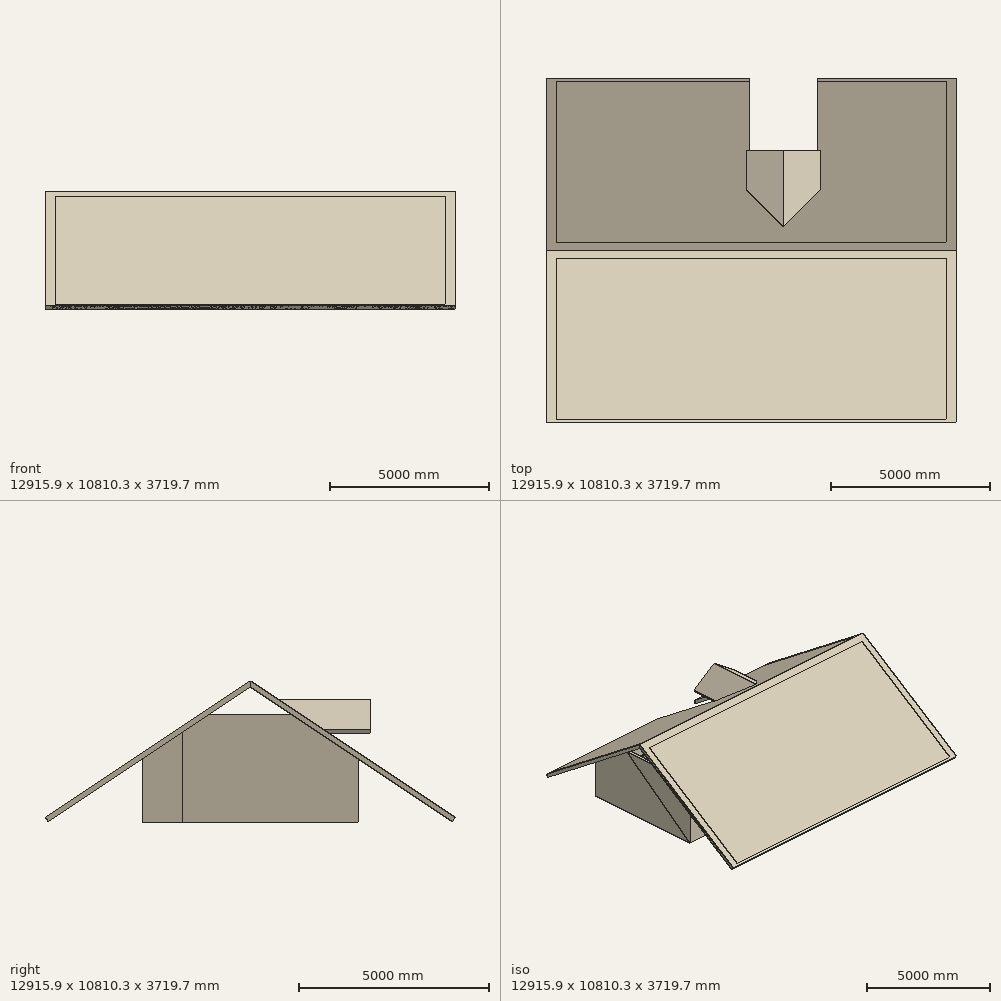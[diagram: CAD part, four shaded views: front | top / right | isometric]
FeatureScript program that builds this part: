
annotation { "Feature Type Name" : "Feature", "Feature Type Description" : "" }
export const myFeature = defineFeature(function(context is Context, id is Id, definition is map)
    precondition{}
    {
        {
            var Q0;
            Q0=qCreatedBy(makeId("Top.planeOp"),FACE);
            cPlane(context, id + "F0", {"entities" : qUnion([Q0]), "cplaneType" : CPlaneType.OFFSET, "offset" : 1 / 406.4 * mm, "oppositeDirection" : true, "width" : 152.4 * mm, "height" : 152.4 * mm});
        }
        {
            var Q0;
            Q0=qCreatedBy(makeId("Top.planeOp"),FACE);
            var sketch = newSketch(context, id + "F1", { "sketchPlane" : qUnion([Q0])});
            skLineSegment(sketch, "E0", {"start": v(0, 0) * mm, "end": v(0, 5448.3) * mm});
            skLineSegment(sketch, "E1", {"start": v(0, 5448.3) * mm, "end": v(12306.3, 5448.3) * mm});
            skLineSegment(sketch, "E2", {"start": v(12306.3, 5448.3) * mm, "end": v(12306.3, 800.1) * mm});
            skLineSegment(sketch, "E3", {"start": v(12306.3, 800.1) * mm, "end": v(9880.6, 800.1) * mm});
            skLineSegment(sketch, "E4", {"start": v(9880.6, 800.1) * mm, "end": v(9880.6, -254) * mm});
            skLineSegment(sketch, "E5", {"start": v(9880.6, -254) * mm, "end": v(3975.1, -254) * mm});
            skLineSegment(sketch, "E6", {"start": v(3975.1, -254) * mm, "end": v(3975.1, 1689.1) * mm});
            skLineSegment(sketch, "E7", {"start": v(3975.1, 1689.1) * mm, "end": v(2006.6, 1689.1) * mm});
            skLineSegment(sketch, "E8", {"start": v(2006.6, 1689.1) * mm, "end": v(2006.6, 0) * mm});
            skLineSegment(sketch, "E9", {"start": v(2006.6, 0) * mm, "end": v(0, 0) * mm});
            skLineSegment(sketch, "E10.0", {"start": v(12153.9, 5295.9) * mm, "end": v(12153.9, 952.5) * mm, "construction": true});
            skLineSegment(sketch, "E10.1", {"start": v(152.4, 5295.9) * mm, "end": v(12153.9, 5295.9) * mm, "construction": true});
            skLineSegment(sketch, "E10.2", {"start": v(12153.9, 952.5) * mm, "end": v(9728.2, 952.5) * mm, "construction": true});
            skLineSegment(sketch, "E10.3", {"start": v(152.4, 152.4) * mm, "end": v(152.4, 5295.9) * mm, "construction": true});
            skLineSegment(sketch, "E10.4", {"start": v(1854.2, 152.4) * mm, "end": v(152.4, 152.4) * mm, "construction": true});
            skLineSegment(sketch, "E10.5", {"start": v(1854.2, 1841.5) * mm, "end": v(1854.2, 152.4) * mm, "construction": true});
            skLineSegment(sketch, "E10.6", {"start": v(9728.2, 952.5) * mm, "end": v(9728.2, -101.6) * mm, "construction": true});
            skLineSegment(sketch, "E10.7", {"start": v(9728.2, -101.6) * mm, "end": v(4127.5, -101.6) * mm, "construction": true});
            skLineSegment(sketch, "E10.8", {"start": v(4127.5, -101.6) * mm, "end": v(4127.5, 1841.5) * mm, "construction": true});
            skLineSegment(sketch, "E10.9", {"start": v(4127.5, 1841.5) * mm, "end": v(1854.2, 1841.5) * mm, "construction": true});
            skLineSegment(sketch, "E11", {"start": v(0, 0) * mm, "end": v(0, -114.3) * mm, "construction": true});
            skLineSegment(sketch, "E12.bottom", {"start": v(7023.1, -101.6) * mm, "end": v(7137.4, -101.6) * mm, "construction": true});
            skLineSegment(sketch, "E12.top", {"start": v(7023.1, 3365.5) * mm, "end": v(7137.4, 3365.5) * mm, "construction": true});
            skLineSegment(sketch, "E12.left", {"start": v(7023.1, -101.6) * mm, "end": v(7023.1, 3365.5) * mm, "construction": true});
            skLineSegment(sketch, "E12.right", {"start": v(7137.4, -101.6) * mm, "end": v(7137.4, 3365.5) * mm, "construction": true});
            skLineSegment(sketch, "E13.bottom", {"start": v(7137.4, 2730.5) * mm, "end": v(9728.2, 2730.5) * mm, "construction": true});
            skLineSegment(sketch, "E13.top", {"start": v(7137.4, 2616.2) * mm, "end": v(9728.2, 2616.2) * mm, "construction": true});
            skLineSegment(sketch, "E13.left", {"start": v(7137.4, 2730.5) * mm, "end": v(7137.4, 2616.2) * mm, "construction": true});
            skLineSegment(sketch, "E13.right", {"start": v(9728.2, 2730.5) * mm, "end": v(9728.2, 2616.2) * mm, "construction": true});
            skLineSegment(sketch, "E14.bottom", {"start": v(9728.2, 952.5) * mm, "end": v(9842.5, 952.5) * mm, "construction": true});
            skLineSegment(sketch, "E14.top", {"start": v(9728.2, 3263.9) * mm, "end": v(9842.5, 3263.9) * mm, "construction": true});
            skLineSegment(sketch, "E14.left", {"start": v(9728.2, 952.5) * mm, "end": v(9728.2, 3263.9) * mm, "construction": true});
            skLineSegment(sketch, "E14.right", {"start": v(9842.5, 952.5) * mm, "end": v(9842.5, 3263.9) * mm, "construction": true});
            skLineSegment(sketch, "E15.bottom", {"start": v(9728.2, 5295.9) * mm, "end": v(9842.5, 5295.9) * mm, "construction": true});
            skLineSegment(sketch, "E15.top", {"start": v(9728.2, 3873.5) * mm, "end": v(9842.5, 3873.5) * mm, "construction": true});
            skLineSegment(sketch, "E15.left", {"start": v(9728.2, 5295.9) * mm, "end": v(9728.2, 3873.5) * mm, "construction": true});
            skLineSegment(sketch, "E15.right", {"start": v(9842.5, 5295.9) * mm, "end": v(9842.5, 3873.5) * mm, "construction": true});
            skLineSegment(sketch, "E16.bottom", {"start": v(12153.9, 2235.2) * mm, "end": v(11239.5, 2235.2) * mm, "construction": true});
            skLineSegment(sketch, "E16.top", {"start": v(12153.9, 2120.9) * mm, "end": v(11239.5, 2120.9) * mm, "construction": true});
            skLineSegment(sketch, "E16.left", {"start": v(12153.9, 2235.2) * mm, "end": v(12153.9, 2120.9) * mm, "construction": true});
            skLineSegment(sketch, "E16.right", {"start": v(11239.5, 2235.2) * mm, "end": v(11239.5, 2120.9) * mm, "construction": true});
            skLineSegment(sketch, "E17.bottom", {"start": v(10439.4, 952.5) * mm, "end": v(10553.7, 952.5) * mm, "construction": true});
            skLineSegment(sketch, "E17.top", {"start": v(10439.4, 2260.6) * mm, "end": v(10553.7, 2260.6) * mm, "construction": true});
            skLineSegment(sketch, "E17.left", {"start": v(10439.4, 952.5) * mm, "end": v(10439.4, 2260.6) * mm, "construction": true});
            skLineSegment(sketch, "E17.right", {"start": v(10553.7, 952.5) * mm, "end": v(10553.7, 2260.6) * mm, "construction": true});
            skLineSegment(sketch, "E18.bottom", {"start": v(10553.7, 2260.6) * mm, "end": v(9842.5, 2260.6) * mm, "construction": true});
            skLineSegment(sketch, "E18.top", {"start": v(10553.7, 2374.9) * mm, "end": v(9842.5, 2374.9) * mm, "construction": true});
            skLineSegment(sketch, "E18.left", {"start": v(10553.7, 2260.6) * mm, "end": v(10553.7, 2374.9) * mm, "construction": true});
            skLineSegment(sketch, "E18.right", {"start": v(9842.5, 2260.6) * mm, "end": v(9842.5, 2374.9) * mm, "construction": true});
            skLineSegment(sketch, "E19.bottom", {"start": v(1854.2, 1841.5) * mm, "end": v(1968.5, 1841.5) * mm, "construction": true});
            skLineSegment(sketch, "E19.top", {"start": v(1854.2, 1879.6) * mm, "end": v(1968.5, 1879.6) * mm, "construction": true});
            skLineSegment(sketch, "E19.left", {"start": v(1854.2, 1841.5) * mm, "end": v(1854.2, 1879.6) * mm, "construction": true});
            skLineSegment(sketch, "E19.right", {"start": v(1968.5, 1841.5) * mm, "end": v(1968.5, 1879.6) * mm, "construction": true});
            skLineSegment(sketch, "E20.bottom", {"start": v(1968.5, 1879.6) * mm, "end": v(965.2, 1879.6) * mm, "construction": true});
            skLineSegment(sketch, "E20.top", {"start": v(1968.5, 1993.9) * mm, "end": v(965.2, 1993.9) * mm, "construction": true});
            skLineSegment(sketch, "E20.left", {"start": v(1968.5, 1879.6) * mm, "end": v(1968.5, 1993.9) * mm, "construction": true});
            skLineSegment(sketch, "E20.right", {"start": v(965.2, 1879.6) * mm, "end": v(965.2, 1993.9) * mm, "construction": true});
            skLineSegment(sketch, "E21.bottom", {"start": v(152.4, 1739.9) * mm, "end": v(850.9, 1739.9) * mm, "construction": true});
            skLineSegment(sketch, "E21.top", {"start": v(152.4, 1625.6) * mm, "end": v(850.9, 1625.6) * mm, "construction": true});
            skLineSegment(sketch, "E21.left", {"start": v(152.4, 1739.9) * mm, "end": v(152.4, 1625.6) * mm, "construction": true});
            skLineSegment(sketch, "E21.right", {"start": v(850.9, 1739.9) * mm, "end": v(850.9, 1625.6) * mm, "construction": true});
            skLineSegment(sketch, "E22.bottom", {"start": v(850.9, 1625.6) * mm, "end": v(965.2, 1625.6) * mm, "construction": true});
            skLineSegment(sketch, "E22.top", {"start": v(850.9, 2438.4) * mm, "end": v(965.2, 2438.4) * mm, "construction": true});
            skLineSegment(sketch, "E22.left", {"start": v(850.9, 1625.6) * mm, "end": v(850.9, 2438.4) * mm, "construction": true});
            skLineSegment(sketch, "E22.right", {"start": v(965.2, 1625.6) * mm, "end": v(965.2, 2438.4) * mm, "construction": true});
            skLineSegment(sketch, "E23.bottom", {"start": v(965.2, 2438.4) * mm, "end": v(635, 2438.4) * mm, "construction": true});
            skLineSegment(sketch, "E23.top", {"start": v(965.2, 2552.7) * mm, "end": v(635, 2552.7) * mm, "construction": true});
            skLineSegment(sketch, "E23.left", {"start": v(965.2, 2438.4) * mm, "end": v(965.2, 2552.7) * mm, "construction": true});
            skLineSegment(sketch, "E23.right", {"start": v(635, 2438.4) * mm, "end": v(635, 2552.7) * mm, "construction": true});
            skLineSegment(sketch, "E24.bottom", {"start": v(635, 2438.4) * mm, "end": v(520.7, 2438.4) * mm, "construction": true});
            skLineSegment(sketch, "E24.top", {"start": v(635, 2895.6) * mm, "end": v(520.7, 2895.6) * mm, "construction": true});
            skLineSegment(sketch, "E24.left", {"start": v(635, 2438.4) * mm, "end": v(635, 2895.6) * mm, "construction": true});
            skLineSegment(sketch, "E24.right", {"start": v(520.7, 2438.4) * mm, "end": v(520.7, 2895.6) * mm, "construction": true});
            skLineSegment(sketch, "E25.bottom", {"start": v(635, 2895.6) * mm, "end": v(152.4, 2895.6) * mm, "construction": true});
            skLineSegment(sketch, "E25.top", {"start": v(635, 3009.9) * mm, "end": v(152.4, 3009.9) * mm, "construction": true});
            skLineSegment(sketch, "E25.left", {"start": v(635, 2895.6) * mm, "end": v(635, 3009.9) * mm, "construction": true});
            skLineSegment(sketch, "E25.right", {"start": v(152.4, 2895.6) * mm, "end": v(152.4, 3009.9) * mm, "construction": true});
            skLineSegment(sketch, "E26", {"start": v(152.4, 152.4) * mm, "end": v(152.4, 1625.6) * mm});
            skLineSegment(sketch, "E27", {"start": v(965.2, 1625.6) * mm, "end": v(152.4, 1625.6) * mm});
            skLineSegment(sketch, "E28", {"start": v(965.2, 1879.6) * mm, "end": v(965.2, 1625.6) * mm});
            skLineSegment(sketch, "E29", {"start": v(1854.2, 1879.6) * mm, "end": v(965.2, 1879.6) * mm});
            skLineSegment(sketch, "E30", {"start": v(1854.2, 152.4) * mm, "end": v(1854.2, 1879.6) * mm});
            skLineSegment(sketch, "E31", {"start": v(152.4, 152.4) * mm, "end": v(1854.2, 152.4) * mm});
            skLineSegment(sketch, "E32", {"start": v(152.4, 1739.9) * mm, "end": v(850.9, 1739.9) * mm});
            skLineSegment(sketch, "E33", {"start": v(850.9, 2438.4) * mm, "end": v(850.9, 1739.9) * mm});
            skLineSegment(sketch, "E34", {"start": v(520.7, 2438.4) * mm, "end": v(850.9, 2438.4) * mm});
            skLineSegment(sketch, "E35", {"start": v(520.7, 2438.4) * mm, "end": v(520.7, 2895.6) * mm});
            skLineSegment(sketch, "E36", {"start": v(152.4, 2895.6) * mm, "end": v(520.7, 2895.6) * mm});
            skLineSegment(sketch, "E37", {"start": v(152.4, 1739.9) * mm, "end": v(152.4, 2895.6) * mm});
            skLineSegment(sketch, "E38", {"start": v(7137.4, 2616.2) * mm, "end": v(7137.4, -101.6) * mm});
            skLineSegment(sketch, "E39", {"start": v(9728.2, -101.6) * mm, "end": v(9728.2, 2616.2) * mm});
            skLineSegment(sketch, "E40", {"start": v(9728.2, -101.6) * mm, "end": v(7137.4, -101.6) * mm});
            skLineSegment(sketch, "E41", {"start": v(7137.4, 2616.2) * mm, "end": v(9728.2, 2616.2) * mm});
            skLineSegment(sketch, "E42", {"start": v(9842.5, 952.5) * mm, "end": v(10439.4, 952.5) * mm});
            skLineSegment(sketch, "E43", {"start": v(10439.4, 2260.6) * mm, "end": v(9842.5, 2260.6) * mm});
            skLineSegment(sketch, "E44", {"start": v(10439.4, 952.5) * mm, "end": v(10439.4, 2260.6) * mm});
            skLineSegment(sketch, "E45", {"start": v(9842.5, 2260.6) * mm, "end": v(9842.5, 952.5) * mm});
            skLineSegment(sketch, "E46", {"start": v(152.4, 5295.9) * mm, "end": v(152.4, 3009.9) * mm});
            skLineSegment(sketch, "E47", {"start": v(635, 3009.9) * mm, "end": v(152.4, 3009.9) * mm});
            skLineSegment(sketch, "E48", {"start": v(635, 2552.7) * mm, "end": v(635, 3009.9) * mm});
            skLineSegment(sketch, "E49", {"start": v(965.2, 2552.7) * mm, "end": v(635, 2552.7) * mm});
            skLineSegment(sketch, "E50", {"start": v(965.2, 1993.9) * mm, "end": v(965.2, 2552.7) * mm});
            skLineSegment(sketch, "E51", {"start": v(1968.5, 1993.9) * mm, "end": v(965.2, 1993.9) * mm});
            skLineSegment(sketch, "E52", {"start": v(1968.5, 1841.5) * mm, "end": v(1968.5, 1993.9) * mm});
            skLineSegment(sketch, "E53", {"start": v(1968.5, 1841.5) * mm, "end": v(4127.5, 1841.5) * mm});
            skLineSegment(sketch, "E54", {"start": v(4127.5, -101.6) * mm, "end": v(4127.5, 1841.5) * mm});
            skLineSegment(sketch, "E55", {"start": v(7023.1, -101.6) * mm, "end": v(4127.5, -101.6) * mm});
            skLineSegment(sketch, "E56", {"start": v(7023.1, 3365.5) * mm, "end": v(7023.1, -101.6) * mm});
            skLineSegment(sketch, "E57", {"start": v(7137.4, 3365.5) * mm, "end": v(7023.1, 3365.5) * mm});
            skLineSegment(sketch, "E58", {"start": v(7137.4, 2730.5) * mm, "end": v(7137.4, 3365.5) * mm});
            skLineSegment(sketch, "E59", {"start": v(9728.2, 2730.5) * mm, "end": v(7137.4, 2730.5) * mm});
            skLineSegment(sketch, "E60", {"start": v(10553.7, 2374.9) * mm, "end": v(9842.5, 2374.9) * mm});
            skLineSegment(sketch, "E61", {"start": v(10553.7, 952.5) * mm, "end": v(10553.7, 2374.9) * mm});
            skLineSegment(sketch, "E62", {"start": v(12153.9, 952.5) * mm, "end": v(10553.7, 952.5) * mm});
            skLineSegment(sketch, "E63", {"start": v(12153.9, 2120.9) * mm, "end": v(12153.9, 952.5) * mm});
            skLineSegment(sketch, "E64", {"start": v(12153.9, 2120.9) * mm, "end": v(11239.5, 2120.9) * mm});
            skLineSegment(sketch, "E65", {"start": v(11239.5, 2235.2) * mm, "end": v(11239.5, 2120.9) * mm});
            skLineSegment(sketch, "E66", {"start": v(12153.9, 2235.2) * mm, "end": v(11239.5, 2235.2) * mm});
            skLineSegment(sketch, "E67", {"start": v(12153.9, 2235.2) * mm, "end": v(12153.9, 5295.9) * mm});
            skLineSegment(sketch, "E68", {"start": v(9842.5, 5295.9) * mm, "end": v(12153.9, 5295.9) * mm});
            skLineSegment(sketch, "E69", {"start": v(9728.2, 5295.9) * mm, "end": v(152.4, 5295.9) * mm});
            skLineSegment(sketch, "E70", {"start": v(9728.2, 2730.5) * mm, "end": v(9728.2, 5295.9) * mm});
            skLineSegment(sketch, "E71", {"start": v(9842.5, 2374.9) * mm, "end": v(9842.5, 5295.9) * mm});
            skSolve(sketch);
        }
        {
            var Q0;
            Q0=qCreatedBy(makeId("Right.planeOp"),FACE);
            var sketch = newSketch(context, id + "F2", { "sketchPlane" : qUnion([Q0])});
            skLineSegment(sketch, "E72", {"start": v(7924.8, 0) * mm, "end": v(2597.15, 3551.77) * mm, "construction": true});
            skLineSegment(sketch, "E73", {"start": v(2597.15, 3551.77) * mm, "end": v(-2730.5, 0) * mm, "construction": true});
            skLineSegment(sketch, "E74", {"start": v(2597.15, 3551.77) * mm, "end": v(2597.15, 3348.57) * mm, "construction": true});
            skLineSegment(sketch, "E75", {"start": v(2901.95, 3348.57) * mm, "end": v(2292.35, 3348.57) * mm, "construction": true});
            skLineSegment(sketch, "E76", {"start": v(5448.3, 0) * mm, "end": v(5448.3, 1651) * mm, "construction": true});
            skLineSegment(sketch, "E77", {"start": v(-254, 0) * mm, "end": v(-254, 1651) * mm, "construction": true});
            skLineSegment(sketch, "E78", {"start": v(7924.8, 0) * mm, "end": v(7924.8, 3551.77) * mm});
            skLineSegment(sketch, "E79", {"start": v(7924.8, 3551.77) * mm, "end": v(-2730.5, 3551.77) * mm});
            skLineSegment(sketch, "E80", {"start": v(-2730.5, 3551.77) * mm, "end": v(-2730.5, 0) * mm});
            skLineSegment(sketch, "E81", {"start": v(3663.95, 2840.57) * mm, "end": v(1530.35, 2840.57) * mm});
            skLineSegment(sketch, "E82", {"start": v(7924.8, 0) * mm, "end": v(3663.95, 2840.57) * mm});
            skLineSegment(sketch, "E83", {"start": v(1530.35, 2840.57) * mm, "end": v(-2730.5, 0) * mm});
            skSolve(sketch);
        }
        {
            var Q0;
            Q0 = qSketchRegion(id + "F1", true);
            var Q1;
            Q1=sQuery(id+"F2.wireOp",VERTEX,"E74.end");
            extrude(context, id + "F3", {"entities" : qUnion([Q0]), "endBound" : BoundingType.UP_TO_VERTEX, "depth" : 2438.4 * mm, "endBoundEntityVertex" : qUnion([Q1]), "offsetDistance" : 25.4 * mm});
        }
        {
            var Q0;
            Q0=qCreatedBy(id+"F0.planeOp",FACE);
            var sketch = newSketch(context, id + "F4", { "sketchPlane" : qUnion([Q0])});
            skLineSegment(sketch, "E84", {"start": v(0, 0) * mm, "end": v(0, 5448.3) * mm});
            skLineSegment(sketch, "E85", {"start": v(0, 5448.3) * mm, "end": v(12306.3, 5448.3) * mm});
            skLineSegment(sketch, "E86", {"start": v(12306.3, 5448.3) * mm, "end": v(12306.3, 800.1) * mm});
            skLineSegment(sketch, "E87", {"start": v(12306.3, 800.1) * mm, "end": v(9880.6, 800.1) * mm});
            skLineSegment(sketch, "E88", {"start": v(9880.6, 800.1) * mm, "end": v(9880.6, -254) * mm});
            skLineSegment(sketch, "E89", {"start": v(9880.6, -254) * mm, "end": v(3975.1, -254) * mm});
            skLineSegment(sketch, "E90", {"start": v(3975.1, -254) * mm, "end": v(3975.1, 1689.1) * mm});
            skLineSegment(sketch, "E91", {"start": v(3975.1, 1689.1) * mm, "end": v(2006.6, 1689.1) * mm});
            skLineSegment(sketch, "E92", {"start": v(2006.6, 1689.1) * mm, "end": v(2006.6, 0) * mm});
            skLineSegment(sketch, "E93", {"start": v(2006.6, 0) * mm, "end": v(0, 0) * mm});
            skSolve(sketch);
        }
        {
            var Q0;
            Q0 = qSketchRegion(id + "F2", true);
            var Q1;
            Q1=sQuery(id+"F1.wireOp",VERTEX,"E2.start");
            extrude(context, id + "F5", {"entities" : qUnion([Q0]), "operationType" : NewBodyOperationType.REMOVE, "endBound" : BoundingType.UP_TO_VERTEX, "depth" : 25.4 * mm, "endBoundEntityVertex" : qUnion([Q1]), "offsetDistance" : 25.4 * mm});
        }
        {
            var Q0;
            Q0=qCreatedBy(makeId("Right.planeOp"),FACE);
            var sketch = newSketch(context, id + "F6", { "sketchPlane" : qUnion([Q0])});
            skLineSegment(sketch, "E94", {"start": v(7924.8, 0) * mm, "end": v(2597.15, 3551.77) * mm});
            skLineSegment(sketch, "E95", {"start": v(2597.15, 3551.77) * mm, "end": v(-2730.5, 0) * mm});
            skLineSegment(sketch, "E96", {"start": v(-2730.5, 0) * mm, "end": v(-2808, 116.24) * mm});
            skLineSegment(sketch, "E97", {"start": v(-2808, 116.24) * mm, "end": v(2597.15, 3719.67) * mm});
            skLineSegment(sketch, "E98", {"start": v(8002.3, 116.24) * mm, "end": v(2597.15, 3719.67) * mm});
            skLineSegment(sketch, "E99", {"start": v(7924.8, 0) * mm, "end": v(8002.3, 116.24) * mm});
            skSolve(sketch);
        }
        {
            var Q0;
            Q0 = qSketchRegion(id + "F6", true);
            var Q1;
            Q1=sQuery(id+"F1.wireOp",VERTEX,"E2.start");
            extrude(context, id + "F7", {"entities" : qUnion([Q0]), "endBound" : BoundingType.UP_TO_VERTEX, "depth" : 25.4 * mm, "endBoundEntityVertex" : qUnion([Q1]), "hasOffset" : true, "offsetDistance" : 304.8 * mm, "offsetOppositeDirection" : true, "hasSecondDirection" : true, "secondDirectionOppositeDirection" : true, "secondDirectionDepth" : 304.8 * mm});
        }
        {
            var Q0;
            Q0=qCreatedBy(makeId("Front.planeOp"),FACE);
            var Q1;
            Q1=sQuery(id+"F2.wireOp",VERTEX,"E76.start");
            cPlane(context, id + "F8", {"entities" : qUnion([Q0, Q1]), "cplaneType" : CPlaneType.PLANE_POINT, "offset" : 25.4 * mm, "width" : 152.4 * mm, "height" : 152.4 * mm});
        }
        {
            var Q0;
            Q0=qCreatedBy(id+"F8.planeOp",FACE);
            var sketch = newSketch(context, id + "F9", { "sketchPlane" : qUnion([Q0])});
            skLineSegment(sketch, "E100.bottom", {"start": v(8229.6, 2336.8) * mm, "end": v(6096, 2336.8) * mm, "construction": true});
            skLineSegment(sketch, "E100.top", {"start": v(8229.6, 0) * mm, "end": v(6096, 0) * mm, "construction": true});
            skLineSegment(sketch, "E100.left", {"start": v(8229.6, 2336.8) * mm, "end": v(8229.6, 0) * mm, "construction": true});
            skLineSegment(sketch, "E100.right", {"start": v(6096, 2336.8) * mm, "end": v(6096, 0) * mm, "construction": true});
            skLineSegment(sketch, "E101", {"start": v(8248.65, 2324.1) * mm, "end": v(7162.8, 3048) * mm, "construction": true});
            skLineSegment(sketch, "E102", {"start": v(7162.8, 3048) * mm, "end": v(6076.95, 2324.1) * mm, "construction": true});
            skLineSegment(sketch, "E103", {"start": v(7467.6, 2844.8) * mm, "end": v(6858, 2844.8) * mm, "construction": true});
            skLineSegment(sketch, "E104", {"start": v(7162.8, 3048) * mm, "end": v(7162.8, 2844.8) * mm, "construction": true});
            skLineSegment(sketch, "E105", {"start": v(8229.6, 0) * mm, "end": v(8229.6, 2336.8) * mm});
            skLineSegment(sketch, "E106", {"start": v(8229.6, 2336.8) * mm, "end": v(7162.8, 3048) * mm});
            skLineSegment(sketch, "E107", {"start": v(7162.8, 3048) * mm, "end": v(6096, 2336.8) * mm});
            skLineSegment(sketch, "E108", {"start": v(6096, 2336.8) * mm, "end": v(6096, 0) * mm});
            skLineSegment(sketch, "E109", {"start": v(6096, 0) * mm, "end": v(8229.6, 0) * mm});
            skSolve(sketch);
        }
        {
            var Q0;
            Q0 = qSketchRegion(id + "F9", true);
            var Q1;
            Q1=makeQuery(id+"F7.opExtrude","SWEPT_FACE",FACE,{"disambiguationData":[OSD([sQuery(id+"F6.wireOp",EDGE,"E94")])]});
            extrude(context, id + "F10", {"entities" : qUnion([Q0]), "operationType" : NewBodyOperationType.REMOVE, "endBound" : BoundingType.UP_TO_SURFACE, "depth" : 25.4 * mm, "endBoundEntityFace" : qUnion([Q1]), "offsetDistance" : 25.4 * mm, "hasSecondDirection" : true, "secondDirectionBound" : BoundingType.THROUGH_ALL, "secondDirectionOppositeDirection" : true, "secondDirectionDepth" : 25.4 * mm});
        }
        {
            var Q0;
            Q0=qCreatedBy(id+"F8.planeOp",FACE);
            var sketch = newSketch(context, id + "F11", { "sketchPlane" : qUnion([Q0])});
            skLineSegment(sketch, "E110", {"start": v(8333.19, 2450.9) * mm, "end": v(7162.8, 3231.16) * mm});
            skLineSegment(sketch, "E111", {"start": v(7162.8, 3231.16) * mm, "end": v(5992.41, 2450.9) * mm});
            skLineSegment(sketch, "E112", {"start": v(5992.41, 2450.9) * mm, "end": v(6076.95, 2324.1) * mm});
            skLineSegment(sketch, "E113", {"start": v(6076.95, 2324.1) * mm, "end": v(7162.8, 3048) * mm});
            skLineSegment(sketch, "E114", {"start": v(7162.8, 3048) * mm, "end": v(8248.65, 2324.1) * mm});
            skLineSegment(sketch, "E115", {"start": v(8248.65, 2324.1) * mm, "end": v(8333.19, 2450.9) * mm});
            skSolve(sketch);
        }
        {
            var Q0;
            Q0 = qSketchRegion(id + "F11", true);
            var Q1;
            Q1=makeQuery(id+"F7.opExtrude","SWEPT_BODY",BODY,{"disambiguationData":[OSD([sQuery(id+"F6.wireOp",EDGE,"E94"),sQuery(id+"F6.wireOp",EDGE,"E95"),sQuery(id+"F6.wireOp",EDGE,"E96"),sQuery(id+"F6.wireOp",EDGE,"E97"),sQuery(id+"F6.wireOp",EDGE,"E98"),sQuery(id+"F6.wireOp",EDGE,"E99")])]});
            extrude(context, id + "F12", {"entities" : qUnion([Q0]), "operationType" : NewBodyOperationType.ADD, "endBound" : BoundingType.UP_TO_BODY, "depth" : 25.4 * mm, "endBoundEntityBody" : qUnion([Q1]), "offsetDistance" : 25.4 * mm, "hasSecondDirection" : true, "secondDirectionOppositeDirection" : true, "secondDirectionDepth" : 304.8 * mm});
        }
    });
